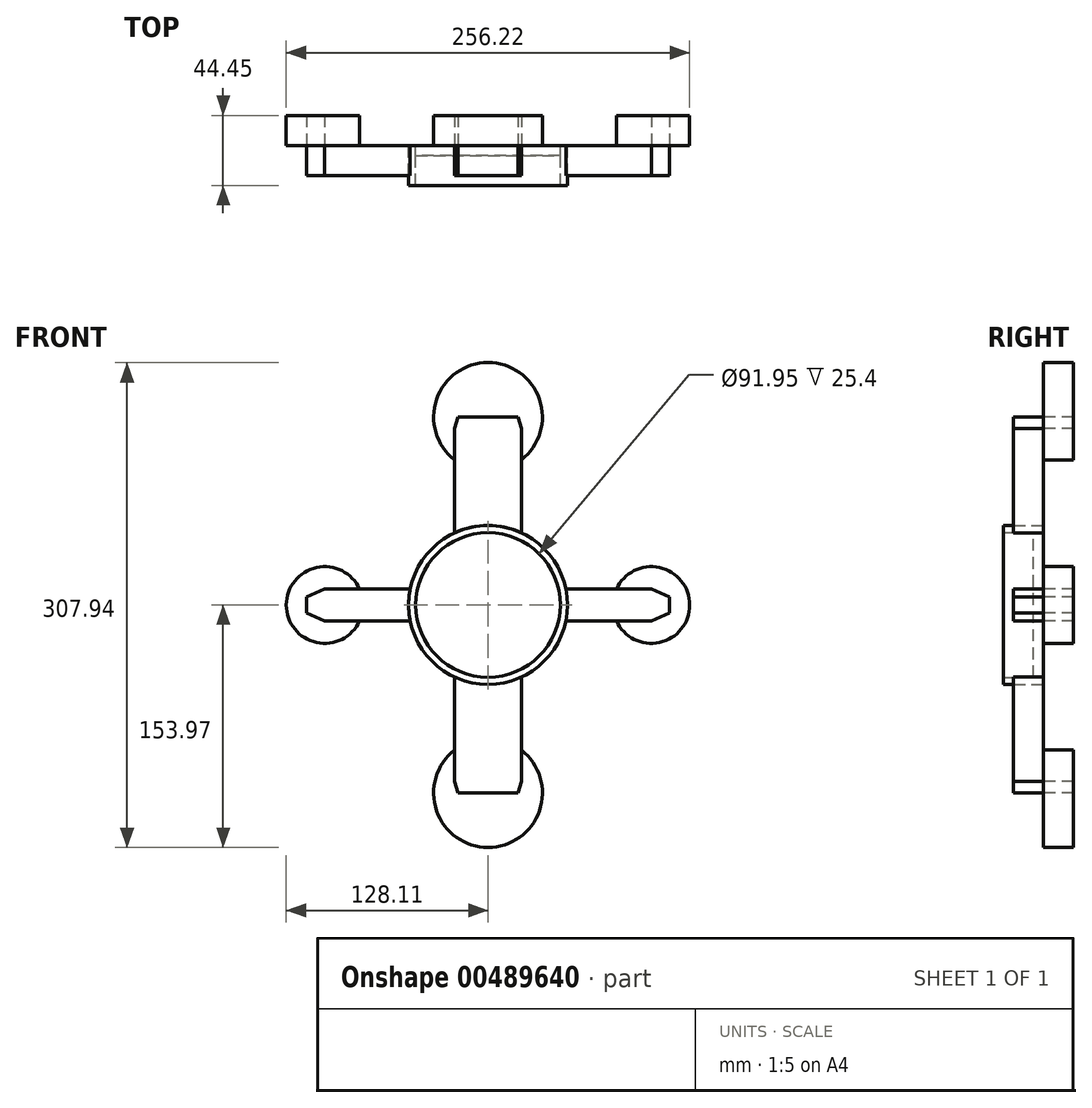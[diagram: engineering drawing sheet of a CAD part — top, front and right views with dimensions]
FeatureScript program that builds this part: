
annotation { "Feature Type Name" : "Feature", "Feature Type Description" : "" }
export const myFeature = defineFeature(function(context is Context, id is Id, definition is map)
    precondition{}
    {
        {
            var Q0;
            Q0=qCreatedBy(makeId("Front.planeOp"),FACE);
            var sketch = newSketch(context, id + "F0", { "sketchPlane" : qUnion([Q0])});
            skCircle(sketch, "E0", {"center": v(0, 0) * mm, "radius": 50.45 * mm});
            skCircle(sketch, "E1", {"center": v(0, 0) * mm, "radius": 45.97 * mm});
            skLineSegment(sketch, "E2", {"start": v(-49.43, 10.07) * mm, "end": v(-103.74, 10.07) * mm});
            skLineSegment(sketch, "E3", {"start": v(-103.74, 10.07) * mm, "end": v(-115.32, 5.05) * mm});
            skLineSegment(sketch, "E4.MirrorCS", {"start": v(49.43, 10.07) * mm, "end": v(103.74, 10.07) * mm});
            skLineSegment(sketch, "E5.MirrorCS", {"start": v(103.74, 10.07) * mm, "end": v(115.32, 5.05) * mm});
            skLineSegment(sketch, "E6.MirrorCS", {"start": v(103.74, -10.07) * mm, "end": v(115.32, -5.05) * mm});
            skLineSegment(sketch, "E7.MirrorCS", {"start": v(49.43, -10.07) * mm, "end": v(103.74, -10.07) * mm});
            skLineSegment(sketch, "E8.MirrorCS", {"start": v(-49.43, -10.07) * mm, "end": v(-103.74, -10.07) * mm});
            skLineSegment(sketch, "E9.MirrorCS", {"start": v(-103.74, -10.07) * mm, "end": v(-115.32, -5.05) * mm});
            skLineSegment(sketch, "E10", {"start": v(-115.32, 5.05) * mm, "end": v(-115.32, -5.05) * mm});
            skLineSegment(sketch, "E11.MirrorCS", {"start": v(115.32, 5.05) * mm, "end": v(115.32, -5.05) * mm});
            skLineSegment(sketch, "E12", {"start": v(-21.23, 45.76) * mm, "end": v(-21.23, 112.08) * mm});
            skLineSegment(sketch, "E13", {"start": v(-21.23, 112.08) * mm, "end": v(-19.2, 119.43) * mm});
            skLineSegment(sketch, "E14", {"start": v(-19.2, 119.43) * mm, "end": v(0, 119.43) * mm});
            skLineSegment(sketch, "E15.MirrorCS", {"start": v(21.23, 45.76) * mm, "end": v(21.23, 112.08) * mm});
            skLineSegment(sketch, "E16.MirrorCS", {"start": v(21.23, 112.08) * mm, "end": v(19.2, 119.43) * mm});
            skLineSegment(sketch, "E17.MirrorCS", {"start": v(19.2, 119.43) * mm, "end": v(0, 119.43) * mm});
            skLineSegment(sketch, "E18.MirrorCS", {"start": v(-21.23, -45.76) * mm, "end": v(-21.23, -112.08) * mm});
            skLineSegment(sketch, "E19.MirrorCS", {"start": v(-21.23, -112.08) * mm, "end": v(-19.2, -119.43) * mm});
            skLineSegment(sketch, "E20.MirrorCS", {"start": v(-19.2, -119.43) * mm, "end": v(0, -119.43) * mm});
            skLineSegment(sketch, "E21.MirrorCS", {"start": v(19.2, -119.43) * mm, "end": v(0, -119.43) * mm});
            skLineSegment(sketch, "E22.MirrorCS", {"start": v(21.23, -112.08) * mm, "end": v(19.2, -119.43) * mm});
            skLineSegment(sketch, "E23.MirrorCS", {"start": v(21.23, -45.76) * mm, "end": v(21.23, -112.08) * mm});
            skCircle(sketch, "E24", {"center": v(103.74, 0) * mm, "radius": 24.37 * mm});
            skCircle(sketch, "E25.MirrorC", {"center": v(-103.74, 0) * mm, "radius": 24.37 * mm});
            skCircle(sketch, "E26", {"center": v(0, 119.43) * mm, "radius": 34.54 * mm});
            skCircle(sketch, "E27.MirrorC", {"center": v(0, -119.43) * mm, "radius": 34.54 * mm});
            skSolve(sketch);
        }
        {
            var Q0;
            Q0=makeQuery(id+"F0.imprint","IMPRINT",FACE,{"disambiguationData":[TD([[makeQuery(id+"F0.imprint","IMPRINT",EDGE,{"derivedFrom":sQuery(id+"F0.wireOp",EDGE,"E1")}),1.0]])]});
            extrude(context, id + "F1", {"entities" : qUnion([Q0]), "depth" : 6.35 * mm});
        }
        {
            var Q0;
            Q0=makeQuery(id+"F0.imprint","IMPRINT",FACE,{"disambiguationData":[TD([[makeQuery(id+"F0.imprint","IMPRINT",EDGE,{"derivedFrom":sQuery(id+"F0.wireOp",EDGE,"E1")}),-1.0]])]});
            extrude(context, id + "F2", {"entities" : qUnion([Q0]), "depth" : 25.4 * mm});
        }
        {
            var Q0;
            {var subQ6=sQuery(id+"F0.wireOp",EDGE,"E3");Q0=makeQuery(id+"F0.imprint","IMPRINT",FACE,{"disambiguationData":[TD([[makeQuery(id+"F0.imprint","IMPRINT",EDGE,{"derivedFrom":subQ6}),1.0]])]});}
            var Q1;
            {var subQ0=sQuery(id+"F0.wireOp",EDGE,"E4.MirrorCS");var subQ1=sQuery(id+"F0.wireOp",EDGE,"E0");var subQ2=makeQuery(id+"F0.imprint","INTERSECT",VERTEX,{"derivedFrom":[subQ1,subQ0]});Q1=makeQuery(id+"F0.imprint","IMPRINT",FACE,{"disambiguationData":[TD([[makeQuery(id+"F0.imprint","IMPRINT",EDGE,{"disambiguationData":[TD([[subQ2,1.0]])],"derivedFrom":subQ1}),-1.0]])]});}
            var Q2;
            {var subQ6=sQuery(id+"F0.wireOp",EDGE,"E5.MirrorCS");Q2=makeQuery(id+"F0.imprint","IMPRINT",FACE,{"disambiguationData":[TD([[makeQuery(id+"F0.imprint","IMPRINT",EDGE,{"derivedFrom":subQ6}),-1.0]])]});}
            var Q3;
            {var subQ0=sQuery(id+"F0.wireOp",EDGE,"E12");var subQ1=sQuery(id+"F0.wireOp",EDGE,"E0");var subQ2=makeQuery(id+"F0.imprint","INTERSECT",VERTEX,{"derivedFrom":[subQ1,subQ0]});Q3=makeQuery(id+"F0.imprint","IMPRINT",FACE,{"disambiguationData":[TD([[makeQuery(id+"F0.imprint","IMPRINT",EDGE,{"disambiguationData":[TD([[subQ2,1.0]])],"derivedFrom":subQ1}),-1.0]])]});}
            var Q4;
            {var subQ4=sQuery(id+"F0.wireOp",EDGE,"E13");Q4=makeQuery(id+"F0.imprint","IMPRINT",FACE,{"disambiguationData":[TD([[makeQuery(id+"F0.imprint","IMPRINT",EDGE,{"derivedFrom":subQ4}),-1.0]])]});}
            var Q5;
            {var subQ0=sQuery(id+"F0.wireOp",EDGE,"E18.MirrorCS");var subQ1=sQuery(id+"F0.wireOp",EDGE,"E0");var subQ2=makeQuery(id+"F0.imprint","INTERSECT",VERTEX,{"derivedFrom":[subQ1,subQ0]});Q5=makeQuery(id+"F0.imprint","IMPRINT",FACE,{"disambiguationData":[TD([[makeQuery(id+"F0.imprint","IMPRINT",EDGE,{"disambiguationData":[TD([[subQ2,-1.0]])],"derivedFrom":subQ1}),-1.0]])]});}
            var Q6;
            {var subQ5=sQuery(id+"F0.wireOp",EDGE,"E19.MirrorCS");Q6=makeQuery(id+"F0.imprint","IMPRINT",FACE,{"disambiguationData":[TD([[makeQuery(id+"F0.imprint","IMPRINT",EDGE,{"derivedFrom":subQ5}),1.0]])]});}
            var Q7;
            {var subQ0=sQuery(id+"F0.wireOp",EDGE,"E2");var subQ1=sQuery(id+"F0.wireOp",EDGE,"E0");var subQ2=makeQuery(id+"F0.imprint","INTERSECT",VERTEX,{"derivedFrom":[subQ1,subQ0]});Q7=makeQuery(id+"F0.imprint","IMPRINT",FACE,{"disambiguationData":[TD([[makeQuery(id+"F0.imprint","IMPRINT",EDGE,{"disambiguationData":[TD([[subQ2,-1.0]])],"derivedFrom":subQ1}),-1.0]])]});}
            extrude(context, id + "F3", {"entities" : qUnion([Q0, Q1, Q2, Q3, Q4, Q5, Q6, Q7]), "depth" : 19.05 * mm});
        }
        {
            var Q0;
            {var subQ4=sQuery(id+"F0.wireOp",EDGE,"E13");Q0=makeQuery(id+"F0.imprint","IMPRINT",FACE,{"disambiguationData":[TD([[makeQuery(id+"F0.imprint","IMPRINT",EDGE,{"derivedFrom":subQ4}),1.0]])]});}
            var Q1;
            {var subQ5=sQuery(id+"F0.wireOp",EDGE,"E19.MirrorCS");Q1=makeQuery(id+"F0.imprint","IMPRINT",FACE,{"disambiguationData":[TD([[makeQuery(id+"F0.imprint","IMPRINT",EDGE,{"derivedFrom":subQ5}),-1.0]])]});}
            var Q2;
            {var subQ4=sQuery(id+"F0.wireOp",EDGE,"E3");Q2=makeQuery(id+"F0.imprint","IMPRINT",FACE,{"disambiguationData":[TD([[makeQuery(id+"F0.imprint","IMPRINT",EDGE,{"derivedFrom":subQ4}),-1.0]])]});}
            var Q3;
            {var subQ4=sQuery(id+"F0.wireOp",EDGE,"E5.MirrorCS");Q3=makeQuery(id+"F0.imprint","IMPRINT",FACE,{"disambiguationData":[TD([[makeQuery(id+"F0.imprint","IMPRINT",EDGE,{"derivedFrom":subQ4}),1.0]])]});}
            extrude(context, id + "F4", {"entities" : qUnion([Q0, Q1, Q2, Q3]), "oppositeDirection" : true, "depth" : 19.05 * mm});
        }
    });
